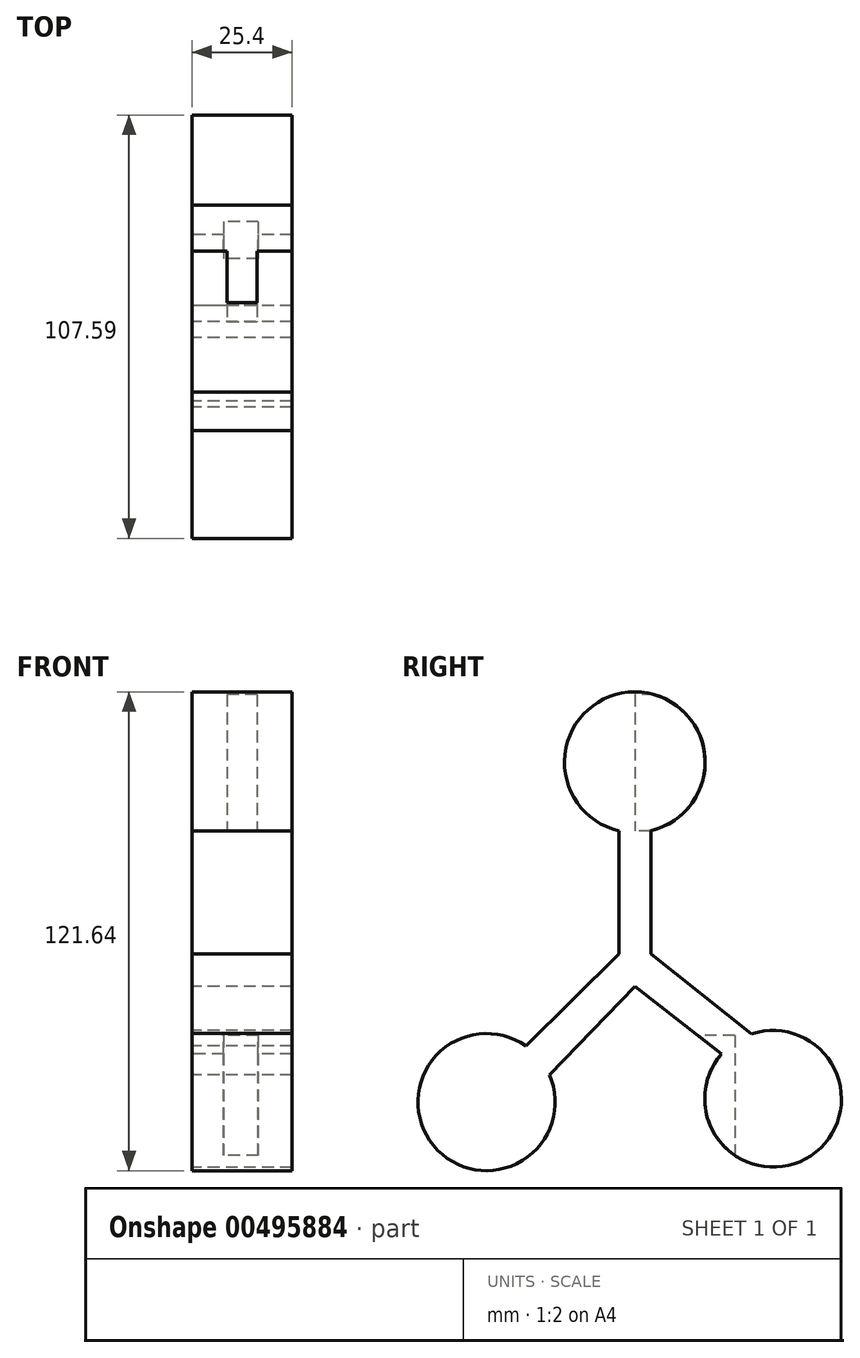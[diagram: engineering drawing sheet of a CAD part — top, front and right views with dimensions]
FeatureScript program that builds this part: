
annotation { "Feature Type Name" : "Feature", "Feature Type Description" : "" }
export const myFeature = defineFeature(function(context is Context, id is Id, definition is map)
    precondition{}
    {
        {
            var Q0;
            Q0=qCreatedBy(makeId("Right.planeOp"),FACE);
            var sketch = newSketch(context, id + "F0", { "sketchPlane" : qUnion([Q0])});
            skCircle(sketch, "E0", {"center": v(0, 48.68) * mm, "radius": 17.87 * mm});
            skCircle(sketch, "E1", {"center": v(35.14, -36.83) * mm, "radius": 17.36 * mm});
            skCircle(sketch, "E2", {"center": v(-37.68, -37.68) * mm, "radius": 17.42 * mm});
            skLineSegment(sketch, "E3.bottom", {"start": v(-4.01, 31.27) * mm, "end": v(4.1, 31.27) * mm});
            skLineSegment(sketch, "E3.top", {"start": v(-4.01, 0) * mm, "end": v(4.1, 0) * mm});
            skLineSegment(sketch, "E3.left", {"start": v(-4.01, 31.27) * mm, "end": v(-4.01, 0) * mm});
            skLineSegment(sketch, "E3.right", {"start": v(4.1, 31.27) * mm, "end": v(4.1, 0) * mm});
            skLineSegment(sketch, "E4", {"start": v(-27.7, -23.4) * mm, "end": v(-4.01, 0) * mm});
            skLineSegment(sketch, "E5", {"start": v(-21.72, -30.7) * mm, "end": v(0, -8.33) * mm});
            skLineSegment(sketch, "E6", {"start": v(0, -8.33) * mm, "end": v(22.05, -25.42) * mm});
            skLineSegment(sketch, "E7", {"start": v(4.1, 0) * mm, "end": v(29.64, -20.36) * mm});
            skSolve(sketch);
        }
        {
            var Q0;
            Q0 = qSketchRegion(id + "F0", true);
            extrude(context, id + "F1", {"entities" : qUnion([Q0]), "depth" : 25.4 * mm});
        }
        {
            var Q0;
            Q0=qCreatedBy(makeId("Front.planeOp"),FACE);
            var sketch = newSketch(context, id + "F2", { "sketchPlane" : qUnion([Q0])});
            skLineSegment(sketch, "E8.bottom", {"start": v(8.89, 65.9) * mm, "end": v(16.5, 65.9) * mm});
            skLineSegment(sketch, "E8.top", {"start": v(8.89, 31.19) * mm, "end": v(16.5, 31.19) * mm});
            skLineSegment(sketch, "E8.left", {"start": v(8.89, 65.9) * mm, "end": v(8.89, 31.19) * mm});
            skLineSegment(sketch, "E8.right", {"start": v(16.5, 65.9) * mm, "end": v(16.5, 31.19) * mm});
            skLineSegment(sketch, "E9.bottom", {"start": v(8.04, -20.74) * mm, "end": v(16.8, -20.74) * mm});
            skLineSegment(sketch, "E9.top", {"start": v(8.04, -55.17) * mm, "end": v(16.8, -55.17) * mm});
            skLineSegment(sketch, "E9.left", {"start": v(8.04, -20.74) * mm, "end": v(8.04, -55.17) * mm});
            skLineSegment(sketch, "E9.right", {"start": v(16.8, -20.74) * mm, "end": v(16.8, -55.17) * mm});
            skLineSegment(sketch, "E10.bottom", {"start": v(16.8, -20.74) * mm, "end": v(8.04, -20.74) * mm});
            skLineSegment(sketch, "E10.top", {"start": v(16.8, -55.17) * mm, "end": v(8.04, -55.17) * mm});
            skLineSegment(sketch, "E11.bottom", {"start": v(16.5, 65.9) * mm, "end": v(8.89, 65.9) * mm});
            skLineSegment(sketch, "E11.top", {"start": v(16.5, 31.19) * mm, "end": v(8.89, 31.19) * mm});
            skSolve(sketch);
        }
        {
            var Q0;
            Q0 = qSketchRegion(id + "F2", true);
            extrude(context, id + "F3", {"entities" : qUnion([Q0]), "operationType" : NewBodyOperationType.REMOVE, "oppositeDirection" : true, "depth" : 25.4 * mm});
        }
        {
            var Q0;
            Q0 = qSketchRegion(id + "F2", true);
            extrude(context, id + "F4", {"entities" : qUnion([Q0]), "operationType" : NewBodyOperationType.REMOVE, "oppositeDirection" : true, "depth" : 25.4 * mm});
        }
        {
            var Q0;
            Q0 = qSketchRegion(id + "F2", true);
            extrude(context, id + "F5", {"entities" : qUnion([Q0]), "operationType" : NewBodyOperationType.REMOVE, "oppositeDirection" : true, "depth" : 25.4 * mm});
        }
    });
